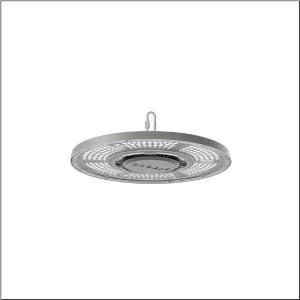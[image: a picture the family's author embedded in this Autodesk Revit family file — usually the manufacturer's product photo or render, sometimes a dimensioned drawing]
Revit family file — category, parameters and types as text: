
# Revit family: highbay_31-s_51hc417a4jmb
name_source: partatom
category: Lighting Fixtures
units: mm (PartAtom-declared; Revit-internal decimal feet)

## family parameters
Cut with Voids When Loaded = No
Host = Face
Light Source = No
Part Type = Normal
Room Calculation Point = No
Round Connector Dimension = Use Diameter
Shared = No

## types (1)
- Highbay 31-S (1 x LED, 20000 lm, 134 W, 4000K)
    Apparent Load = 134 VA
    CIE Flux Codes = 95 98 100 100 100
    Color Rendering = 80
    Color Temperature = 4000K
    Default Elevation = 1800 mm
    Description = Highbay 31-S, high bay luminaire, primary light control with lens, of PC, primary optical cover: cover panel, of PC, transparent, light emission: direct distribution, primary light characteristic: rotationally symmetric, installation type: suspended mounting, surface-mounted, LED, rated luminous flux: 20.000lm, luminous efficacy: 150lm/W, light colour: 840, colour temperature: 4000K, control gear: ON/OFF, with cable, 3x 1.0mm², free wire ends, mains connection: 220..240V, AC, 50/60Hz, cable length: 1,5m, rated input power: 134W, housing, rotationally symmetric, of diecast aluminium, powder-coated, grey aluminium (RAL 9007), with hook on luminaire side, incl. screw, diameter: 339mm, protection rating (complete): IP65, insulation class (complete): insulation class I (protective earthing), certification: CE, ENEC, UKCA, protection symbol: D, impact resistance: IK08, permissible operating ambient temperature: -30..+45°C, corresponds to IFS (International Featured Standards) requirements for safety and quality in the food industry, packaging unit: 1 piece
    Height = 141 mm
    Lamp = 1 x LED
    Lamp Light Flux = 20000 lm
    Lamp Power = 134 W
    Lamp count = 1
    Length = 339 mm
    Luminous efficacy = 149 lm/W
    Manufacturer = Siteco
    ModVariant = No
    Model = 51HC417A4JMB
    Mounting Place = Ceiling
    Mounting Type = Pendant
    Number of Poles = 1
    OnlyDefault = Yes
    Power Factor = 1
    Product Name = Highbay 31-S
    Product group = high bay luminaire
    ProductGroupID = 902
    Protection Class = Protection class I
    Protection Degree = IP 65
    RLX_Detail_Level = 1
    RLX_Emergency_Light_Flux = 0 lm
    RLX_Emergency_Type = 0
    RLX_Emergency_Type_DB = No
    RlxData = <blob elided: 107009 chars, md5=d0e9bbc9>
    Socket = socket
    Standby Power = 0 W
    System Light Flux = 20000 lm
    System Power = 134 W
    Type Comments = Product without accessories
    Type Image = l_1007237.jpg
    URL = http://relux.com
    VarID = ---
    Voltage = 0 V
    Weight = 0.00 kg
    Width = 0 mm  [stored 0 ft]

note: [stored X ft] marks values corroborated as IEEE doubles in the binary element streams (Revit-internal decimal feet)

## geometry (parser evidence)
native form markers: Blend x4, Sweep x11
no freeform markers — native parametric forms only
